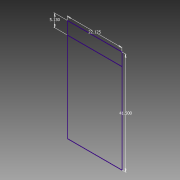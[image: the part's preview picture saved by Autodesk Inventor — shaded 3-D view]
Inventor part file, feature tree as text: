
AUTODESK INVENTOR PART (.ipt)
format: ipt  version: 2013 (Build 170138000, 138)  size: 62,464 bytes
history: native  units: in
note: dims shown in document units (in); Inventor stores cm internally (conversion verified against a paired STEP export)
features: sketch x1
ambient origin geometry x8: Origin, YZ Plane, XZ Plane, XY Plane, X Axis, Y Axis, Z Axis, Center Point
feature tree (1):
  sketch  "Sketch1"  dims[d0=22.125in d1=41.5in d2=5.13in]
